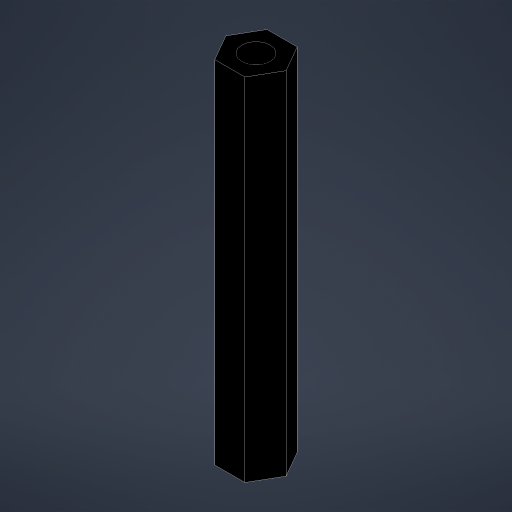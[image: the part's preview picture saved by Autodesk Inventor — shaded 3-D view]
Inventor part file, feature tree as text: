
AUTODESK INVENTOR PART (.ipt)
format: ipt  version: 2025 (Build 290162010, 162A)  size: 171,008 bytes
history: native  units: mm
features: extrude x1, sketch x1
ambient origin geometry x8: Origin, YZ Plane, XZ Plane, XY Plane, X Axis, Y Axis, Z Axis, Center Point
bodies: Solid1 (feature_tree)
feature tree (2):
  extrude  "Extrusion1"  Depth=37.0mm
  sketch  "Sketch1"  dims[d0=5.5mm d1=3.0mm d2=37.0mm d3=0.0mm d4=0.5mm d5=0.872665mm]
